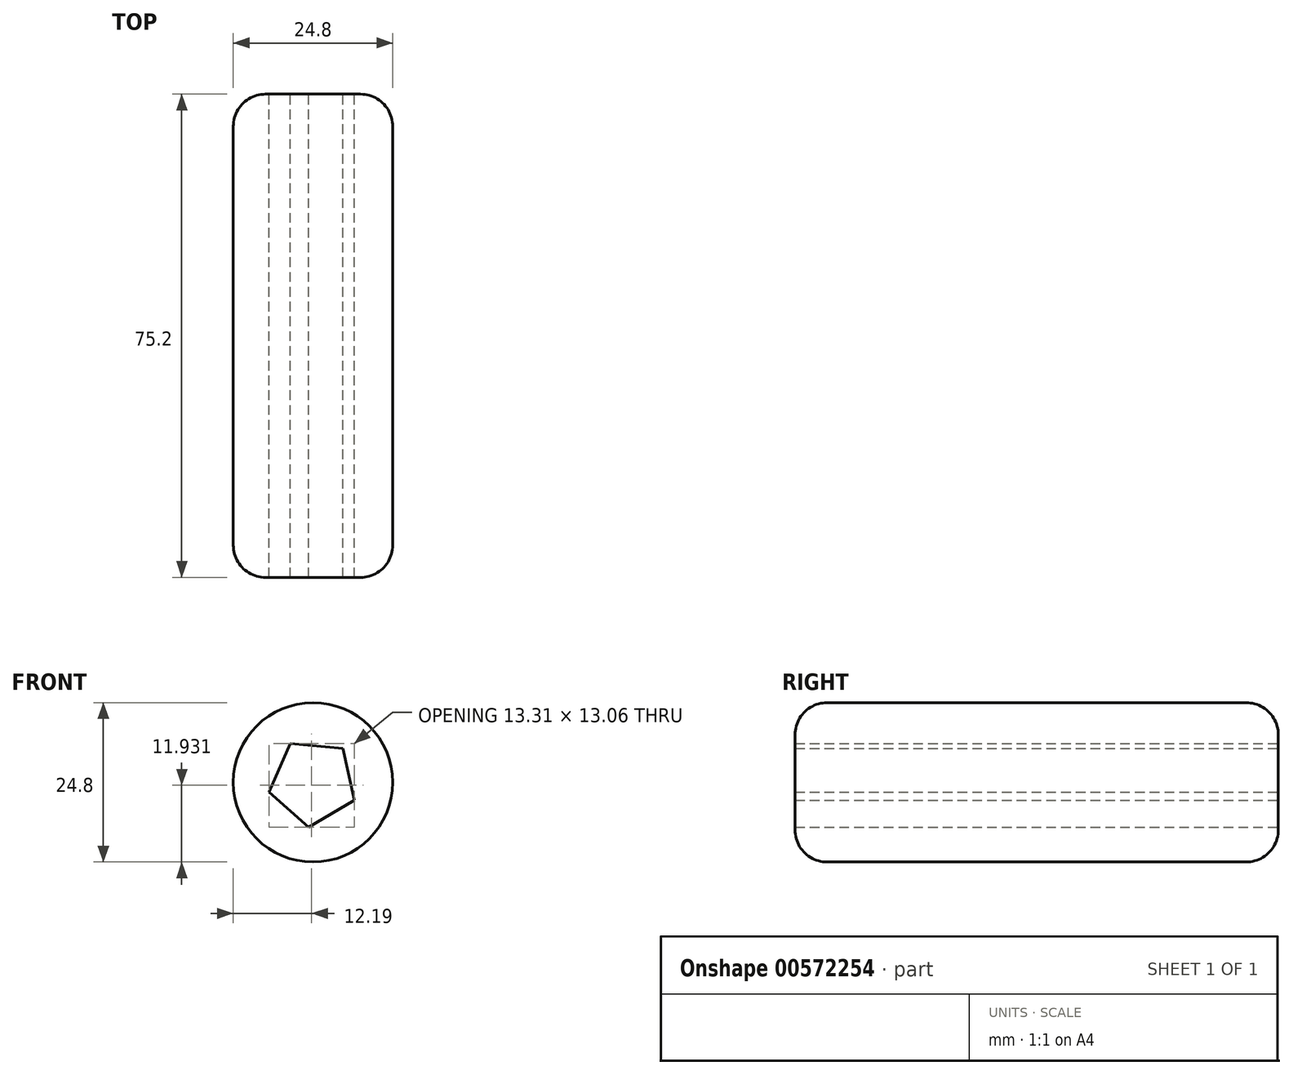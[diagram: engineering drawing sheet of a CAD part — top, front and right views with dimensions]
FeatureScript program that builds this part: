
annotation { "Feature Type Name" : "Feature", "Feature Type Description" : "" }
export const myFeature = defineFeature(function(context is Context, id is Id, definition is map)
    precondition{}
    {
        {
            var Q0;
            Q0=qCreatedBy(makeId("Front.planeOp"),FACE);
            var sketch = newSketch(context, id + "F0", { "sketchPlane" : qUnion([Q0])});
            skCircle(sketch, "E0", {"center": v(0, 0) * mm, "radius": 12.4 * mm});
            skSolve(sketch);
        }
        {
            var Q0;
            Q0 = qSketchRegion(id + "F0", true);
            extrude(context, id + "F1", {"entities" : qUnion([Q0]), "depth" : 75.2 * mm, "offsetDistance" : 25 * mm});
        }
        {
            var Q0;
            Q0=makeQuery(id+"F1.opExtrude","CAP_EDGE",EDGE,{"disambiguationData":[OSD([sQuery(id+"F0.wireOp",EDGE,"E0")])],"isStart":false});
            var Q1;
            Q1=makeQuery(id+"F1.opExtrude","SWEPT_FACE",FACE,{"disambiguationData":[OSD([sQuery(id+"F0.wireOp",EDGE,"E0")])]});
            fillet(context, id + "F2", {"entities" : qUnion([Q0, Q1]), "radius" : 5 * mm, "tangentPropagation" : true, "allowEdgeOverflow" : false});
        }
        {
            var Q0;
            Q0=qCreatedBy(makeId("Front.planeOp"),FACE);
            var sketch = newSketch(context, id + "F3", { "sketchPlane" : qUnion([Q0])});
            skCircle(sketch, "E1.cCircle", {"center": v(0, 0) * mm, "radius": 5.69 * mm, "construction": true});
            skLineSegment(sketch, "E1.0", {"start": v(6.45, -2.8) * mm, "end": v(-0.68, -7) * mm});
            skLineSegment(sketch, "E1.1", {"start": v(-0.68, -7) * mm, "end": v(-6.87, -1.52) * mm});
            skLineSegment(sketch, "E1.2", {"start": v(-6.87, -1.52) * mm, "end": v(-3.57, 6.06) * mm});
            skLineSegment(sketch, "E1.3", {"start": v(-3.57, 6.06) * mm, "end": v(4.66, 5.26) * mm});
            skLineSegment(sketch, "E1.4", {"start": v(4.66, 5.26) * mm, "end": v(6.45, -2.8) * mm});
            skPoint(sketch, "E1.0.midPoint", {"position": v(2.88, -4.9) * mm});
            skSolve(sketch);
        }
        {
            var Q0;
            Q0 = qSketchRegion(id + "F3", true);
            extrude(context, id + "F4", {"entities" : qUnion([Q0]), "operationType" : NewBodyOperationType.REMOVE, "depth" : 95 * mm, "offsetDistance" : 25 * mm});
        }
    });
